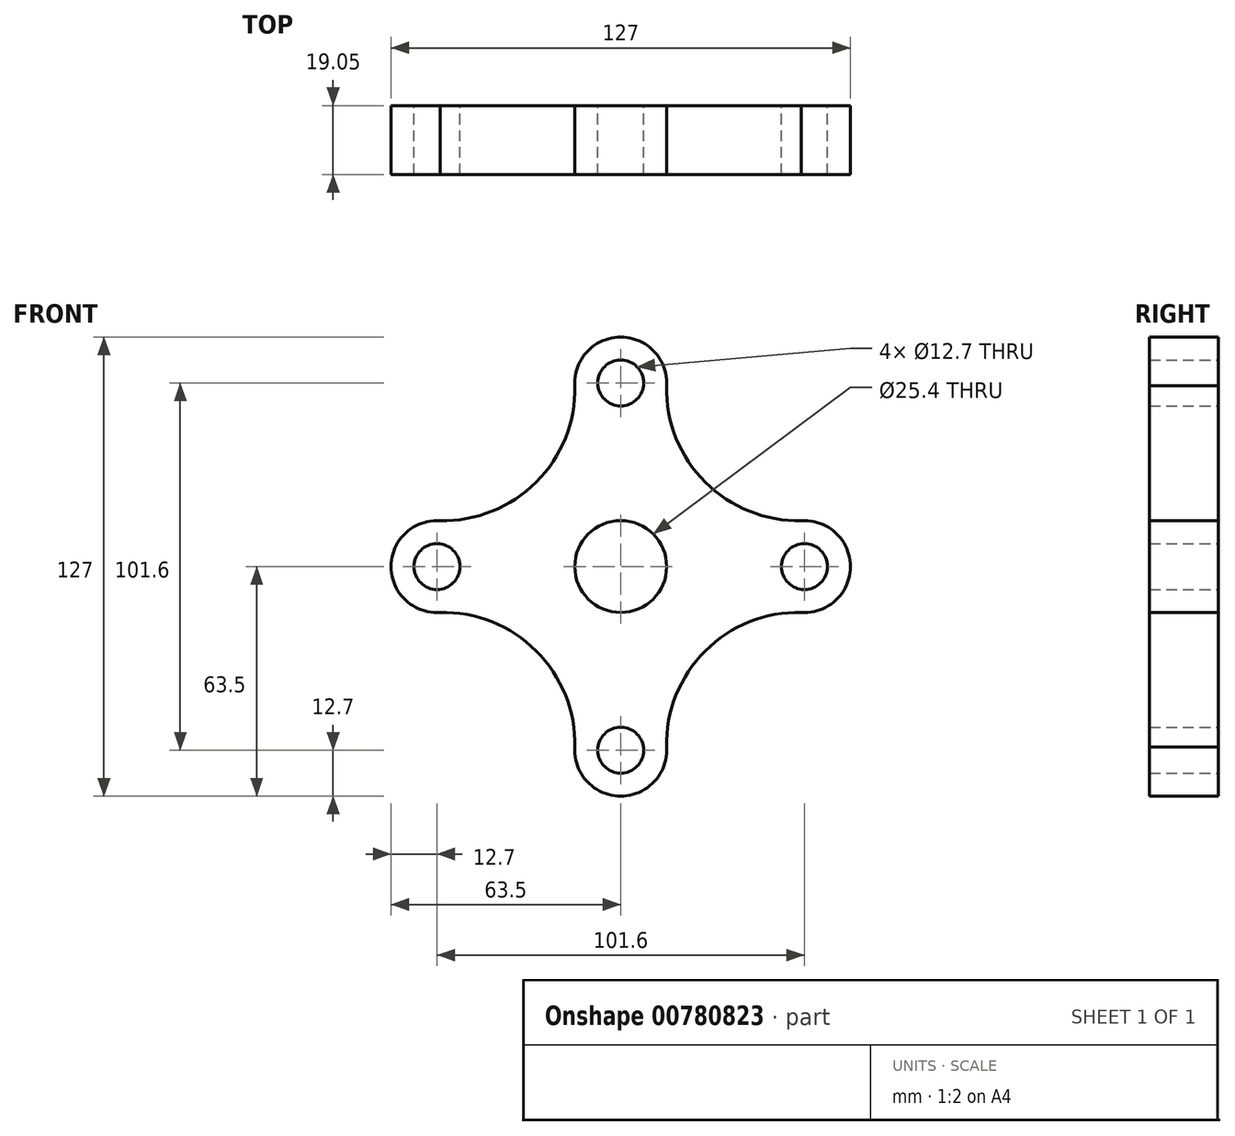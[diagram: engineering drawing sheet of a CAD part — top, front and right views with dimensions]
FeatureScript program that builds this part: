
annotation { "Feature Type Name" : "Feature", "Feature Type Description" : "" }
export const myFeature = defineFeature(function(context is Context, id is Id, definition is map)
    precondition{}
    {
        {
            var Q0;
            Q0=qCreatedBy(makeId("Front.planeOp"),FACE);
            var sketch = newSketch(context, id + "F0", { "sketchPlane" : qUnion([Q0])});
            skCircle(sketch, "E0", {"center": v(0, 0) * mm, "radius": 12.7 * mm});
            skCircle(sketch, "E1", {"center": v(0, 50.8) * mm, "radius": 6.35 * mm});
            skCircle(sketch, "E2", {"center": v(0, -50.8) * mm, "radius": 6.35 * mm});
            skCircle(sketch, "E3", {"center": v(-50.8, 0) * mm, "radius": 6.35 * mm});
            skCircle(sketch, "E4", {"center": v(50.8, 0) * mm, "radius": 6.35 * mm});
            skArc(sketch, "E5", {"start": v(12.67, 49.97) * mm, "mid": v(0, 63.5) * mm, "end": v(-12.67, 49.97) * mm});
            skArc(sketch, "E6", {"start": v(49.97, -12.67) * mm, "mid": v(63.5, 0) * mm, "end": v(49.97, 12.67) * mm});
            skArc(sketch, "E7", {"start": v(-12.67, -49.97) * mm, "mid": v(0, -63.5) * mm, "end": v(12.67, -49.97) * mm});
            skArc(sketch, "E8", {"start": v(-49.97, 12.67) * mm, "mid": v(-63.5, 0) * mm, "end": v(-49.97, -12.67) * mm});
            skLineSegment(sketch, "E9", {"start": v(-50.8, -12.7) * mm, "end": v(-50.8, -19.76) * mm});
            skArc(sketch, "E10", {"start": v(-50.8, 12.7) * mm, "mid": v(-23.36, 23.36) * mm, "end": v(-12.7, 50.8) * mm});
            skArc(sketch, "E11", {"start": v(12.7, 50.8) * mm, "mid": v(23.36, 23.36) * mm, "end": v(50.8, 12.7) * mm});
            skArc(sketch, "E12", {"start": v(-12.7, -50.8) * mm, "mid": v(-23.36, -23.36) * mm, "end": v(-50.8, -12.7) * mm});
            skArc(sketch, "E13", {"start": v(50.8, -12.7) * mm, "mid": v(23.36, -23.36) * mm, "end": v(12.7, -50.8) * mm});
            skPoint(sketch, "E14.orphan", {"position": v(-27.21, 50.8) * mm});
            skPoint(sketch, "E15.orphan", {"position": v(-50.8, 18.43) * mm});
            skPoint(sketch, "E16.trimOffspring.end.orphan", {"position": v(-27.21, -50.8) * mm});
            skPoint(sketch, "E17.orphan", {"position": v(50.8, -19.76) * mm});
            skPoint(sketch, "E18.orphan", {"position": v(50.8, 18.43) * mm});
            skSolve(sketch);
        }
        {
            var Q0;
            Q0 = qSketchRegion(id + "F0", true);
            extrude(context, id + "F1", {"entities" : qUnion([Q0]), "depth" : 19.05 * mm, "offsetDistance" : 25.4 * mm});
        }
    });
